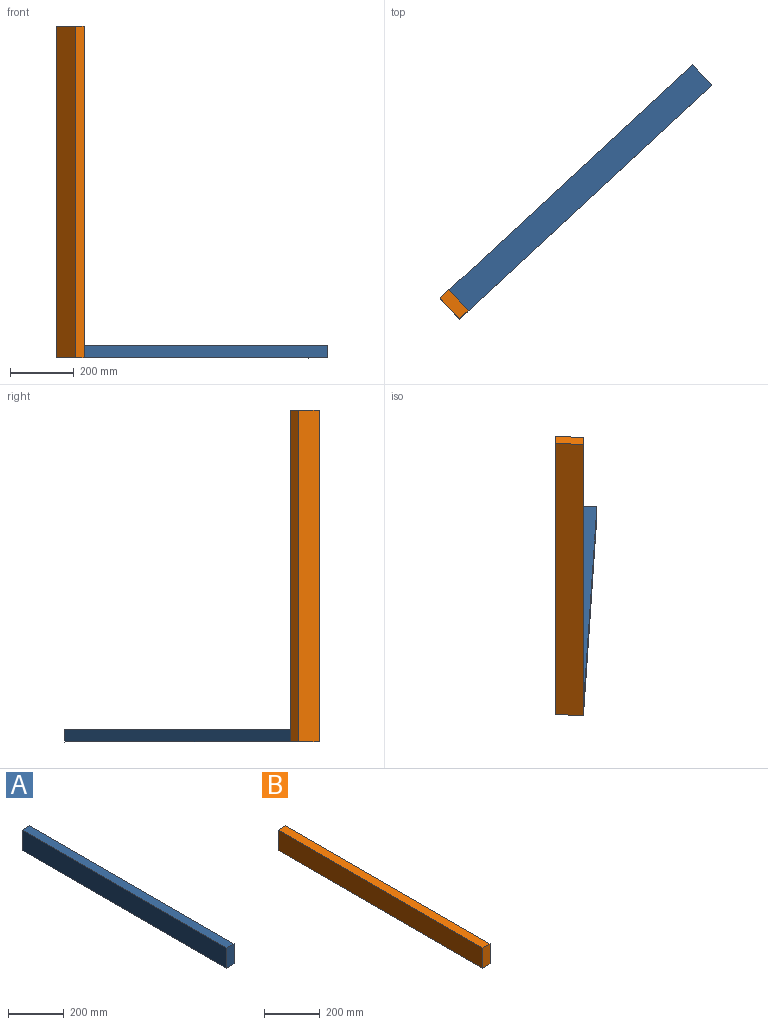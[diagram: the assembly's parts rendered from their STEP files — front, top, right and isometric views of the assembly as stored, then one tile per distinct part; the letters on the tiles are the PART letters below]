
ASSEMBLY  parts=2 mates=1
PART A: 6 faces, bbox 38.1x1041.4x88.9 mm
  f0: plane 1041.4x38.1mm, normal (0,0,-1), area 39677.3mm2, adj f1,f3,f4,f5
  f1: plane 1041.4x88.9mm, normal (1,0,0), area 92580.5mm2, adj f0,f2,f4,f5
  f2: plane 1041.4x38.1mm, normal (0,0,1), area 39677.3mm2, adj f1,f3,f4,f5
  f3: plane 1041.4x88.9mm, normal (-1,0,0), area 92580.5mm2, adj f0,f2,f4,f5
  f4: plane 88.9x38.1mm, normal (0,-1,0), area 3387.1mm2, adj f0,f1,f2,f3
  f5: plane 88.9x38.1mm, normal (0,1,0), area 3387.1mm2, adj f0,f1,f2,f3
PART B: 6 faces, bbox 38.1x1041.4x88.9 mm
  f0: plane 1041.4x38.1mm, normal (0,0,-1), area 39677.3mm2, adj f1,f3,f4,f5
  f1: plane 1041.4x88.9mm, normal (1,0,0), area 92580.5mm2, adj f0,f2,f4,f5
  f2: plane 1041.4x38.1mm, normal (0,0,1), area 39677.3mm2, adj f1,f3,f4,f5
  f3: plane 1041.4x88.9mm, normal (-1,0,0), area 92580.5mm2, adj f0,f2,f4,f5
  f4: plane 88.9x38.1mm, normal (0,-1,0), area 3387.1mm2, adj f0,f1,f2,f3
  f5: plane 88.9x38.1mm, normal (0,1,0), area 3387.1mm2, adj f0,f1,f2,f3
PLACE A rot(axis=(-0.37,-0.85,-0.37),99.2deg) t=(-435.24,609.27,398.96)mm
PLACE B rot(axis=(-0.27,0.68,-0.68),150.1deg) t=(-1311.99,23.53,437.06)mm fixed
MATE revolute B.f0 <-> A.f2  axis (-0.68,0.73,0) through (-1286.12,-4.44,437.06)mm
